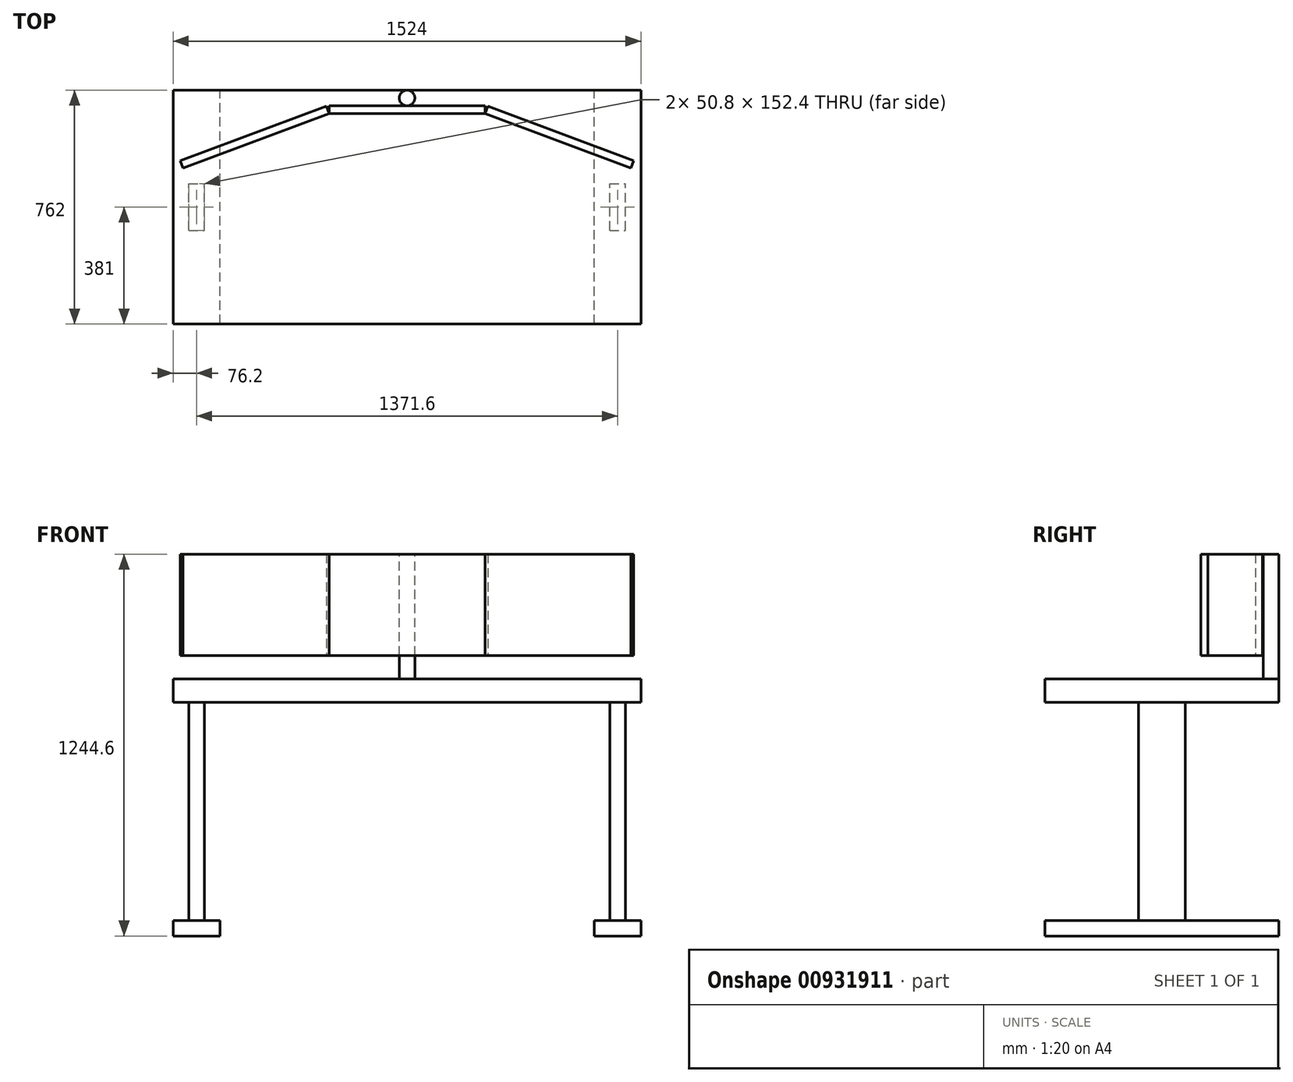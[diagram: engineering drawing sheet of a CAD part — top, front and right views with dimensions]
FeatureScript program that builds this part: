
annotation { "Feature Type Name" : "Feature", "Feature Type Description" : "" }
export const myFeature = defineFeature(function(context is Context, id is Id, definition is map)
    precondition{}
    {
        {
            var Q0;
            Q0=qCreatedBy(makeId("Top.planeOp"),FACE);
            var sketch = newSketch(context, id + "F0", { "sketchPlane" : qUnion([Q0])});
            skLineSegment(sketch, "E0.bottom", {"start": v(0, 0) * mm, "end": v(1524, 0) * mm});
            skLineSegment(sketch, "E0.top", {"start": v(0, -762) * mm, "end": v(1524, -762) * mm});
            skLineSegment(sketch, "E0.left", {"start": v(0, 0) * mm, "end": v(0, -762) * mm});
            skLineSegment(sketch, "E0.right", {"start": v(1524, 0) * mm, "end": v(1524, -762) * mm});
            skSolve(sketch);
        }
        {
            var Q0;
            Q0 = qSketchRegion(id + "F0", true);
            extrude(context, id + "F1", {"entities" : qUnion([Q0]), "depth" : 76.2 * mm, "offsetDistance" : 25.4 * mm});
        }
        {
            var Q0;
            Q0=qCreatedBy(makeId("Top.planeOp"),FACE);
            var sketch = newSketch(context, id + "F2", { "sketchPlane" : qUnion([Q0])});
            skLineSegment(sketch, "E1.bottom", {"start": v(50.8, -457.2) * mm, "end": v(101.6, -457.2) * mm});
            skLineSegment(sketch, "E1.top", {"start": v(50.8, -304.8) * mm, "end": v(101.6, -304.8) * mm});
            skLineSegment(sketch, "E1.left", {"start": v(50.8, -457.2) * mm, "end": v(50.8, -304.8) * mm});
            skLineSegment(sketch, "E1.right", {"start": v(101.6, -457.2) * mm, "end": v(101.6, -304.8) * mm});
            skLineSegment(sketch, "E2.bottom", {"start": v(1422.4, -457.2) * mm, "end": v(1473.2, -457.2) * mm});
            skLineSegment(sketch, "E2.top", {"start": v(1422.4, -304.8) * mm, "end": v(1473.2, -304.8) * mm});
            skLineSegment(sketch, "E2.left", {"start": v(1422.4, -457.2) * mm, "end": v(1422.4, -304.8) * mm});
            skLineSegment(sketch, "E2.right", {"start": v(1473.2, -457.2) * mm, "end": v(1473.2, -304.8) * mm});
            skSolve(sketch);
        }
        {
            var Q0;
            Q0 = qSketchRegion(id + "F2", true);
            extrude(context, id + "F3", {"entities" : qUnion([Q0]), "operationType" : NewBodyOperationType.ADD, "oppositeDirection" : true, "depth" : 711.2 * mm, "offsetDistance" : 25.4 * mm});
        }
        {
            var Q0;
            Q0=qCreatedBy(makeId("Front.planeOp"),FACE);
            var sketch = newSketch(context, id + "F4", { "sketchPlane" : qUnion([Q0])});
            skLineSegment(sketch, "E3.bottom", {"start": v(1524, -711.2) * mm, "end": v(1371.6, -711.2) * mm});
            skLineSegment(sketch, "E3.top", {"start": v(1524, -762) * mm, "end": v(1371.6, -762) * mm});
            skLineSegment(sketch, "E3.left", {"start": v(1524, -711.2) * mm, "end": v(1524, -762) * mm});
            skLineSegment(sketch, "E3.right", {"start": v(1371.6, -711.2) * mm, "end": v(1371.6, -762) * mm});
            skLineSegment(sketch, "E4.bottom", {"start": v(152.4, -711.2) * mm, "end": v(0, -711.2) * mm});
            skLineSegment(sketch, "E4.top", {"start": v(152.4, -762) * mm, "end": v(0, -762) * mm});
            skLineSegment(sketch, "E4.left", {"start": v(152.4, -711.2) * mm, "end": v(152.4, -762) * mm});
            skLineSegment(sketch, "E4.right", {"start": v(0, -711.2) * mm, "end": v(0, -762) * mm});
            skSolve(sketch);
        }
        {
            var Q0;
            Q0 = qSketchRegion(id + "F4", true);
            extrude(context, id + "F5", {"entities" : qUnion([Q0]), "operationType" : NewBodyOperationType.ADD, "depth" : 762 * mm, "offsetDistance" : 25.4 * mm});
        }
        {
            var Q0;
            Q0=qCreatedBy(makeId("Top.planeOp"),FACE);
            cPlane(context, id + "F6", {"entities" : qUnion([Q0]), "cplaneType" : CPlaneType.OFFSET, "offset" : 152.4 * mm, "width" : 152.4 * mm, "height" : 152.4 * mm});
        }
        {
            var Q0;
            Q0=qCreatedBy(id+"F6.planeOp",FACE);
            var sketch = newSketch(context, id + "F7", { "sketchPlane" : qUnion([Q0])});
            skLineSegment(sketch, "E5", {"start": v(23.24, -230.2) * mm, "end": v(499.1, -52.4) * mm});
            skLineSegment(sketch, "E6", {"start": v(499.1, -52.4) * mm, "end": v(508, -76.2) * mm});
            skLineSegment(sketch, "E7", {"start": v(508, -76.2) * mm, "end": v(32.13, -254) * mm});
            skLineSegment(sketch, "E8", {"start": v(32.13, -254) * mm, "end": v(23.24, -230.2) * mm});
            skLineSegment(sketch, "E9.bottom", {"start": v(508, -50.8) * mm, "end": v(1016, -50.8) * mm});
            skLineSegment(sketch, "E9.top", {"start": v(508, -76.2) * mm, "end": v(1016, -76.2) * mm});
            skLineSegment(sketch, "E9.left", {"start": v(508, -50.8) * mm, "end": v(508, -76.2) * mm});
            skLineSegment(sketch, "E9.right", {"start": v(1016, -50.8) * mm, "end": v(1016, -76.2) * mm});
            skLineSegment(sketch, "E10", {"start": v(1024.89, -52.4) * mm, "end": v(1500.76, -230.2) * mm});
            skLineSegment(sketch, "E11", {"start": v(1500.76, -230.2) * mm, "end": v(1491.87, -254) * mm});
            skLineSegment(sketch, "E12", {"start": v(1491.87, -254) * mm, "end": v(1016, -76.2) * mm});
            skLineSegment(sketch, "E13", {"start": v(1016, -76.2) * mm, "end": v(1024.89, -52.4) * mm});
            skCircle(sketch, "E14", {"center": v(762, -25.4) * mm, "radius": 25.4 * mm});
            skPoint(sketch, "E14.centerSnap0", {"position": v(762, -50.8) * mm});
            skSolve(sketch);
        }
        {
            var Q0;
            {var subQ0=sQuery(id+"F7.wireOp",EDGE,"E14");Q0=makeQuery(id+"F7.imprint","IMPRINT",FACE,{"disambiguationData":[TD([[makeQuery(id+"F7.imprint","IMPRINT",EDGE,{"disambiguationData":[TD([[makeQuery(id+"F7.imprint","INTERSECT",VERTEX,{"derivedFrom":[sQuery(id+"F7.wireOp",EDGE,"E9.bottom"),subQ0]}),-1.0]])],"derivedFrom":subQ0}),1.0]])]});}
            extrude(context, id + "F8", {"entities" : qUnion([Q0]), "operationType" : NewBodyOperationType.ADD, "oppositeDirection" : true, "depth" : 76.2 * mm, "offsetDistance" : 25.4 * mm, "hasSecondDirection" : true, "secondDirectionOppositeDirection" : false, "secondDirectionDepth" : 330.2 * mm});
        }
        {
            var Q0;
            Q0=makeQuery(id+"F7.imprint","IMPRINT",FACE,{"disambiguationData":[TD([[makeQuery(id+"F7.imprint","IMPRINT",EDGE,{"derivedFrom":sQuery(id+"F7.wireOp",EDGE,"E5")}),-1.0]])]});
            var Q1;
            Q1=makeQuery(id+"F7.imprint","IMPRINT",FACE,{"disambiguationData":[TD([[makeQuery(id+"F7.imprint","IMPRINT",EDGE,{"derivedFrom":sQuery(id+"F7.wireOp",EDGE,"E9.top")}),1.0]])]});
            var Q2;
            Q2=makeQuery(id+"F7.imprint","IMPRINT",FACE,{"disambiguationData":[TD([[makeQuery(id+"F7.imprint","IMPRINT",EDGE,{"derivedFrom":sQuery(id+"F7.wireOp",EDGE,"E10")}),-1.0]])]});
            extrude(context, id + "F9", {"entities" : qUnion([Q0, Q1, Q2]), "depth" : 330.2 * mm, "offsetDistance" : 25.4 * mm});
        }
    });
